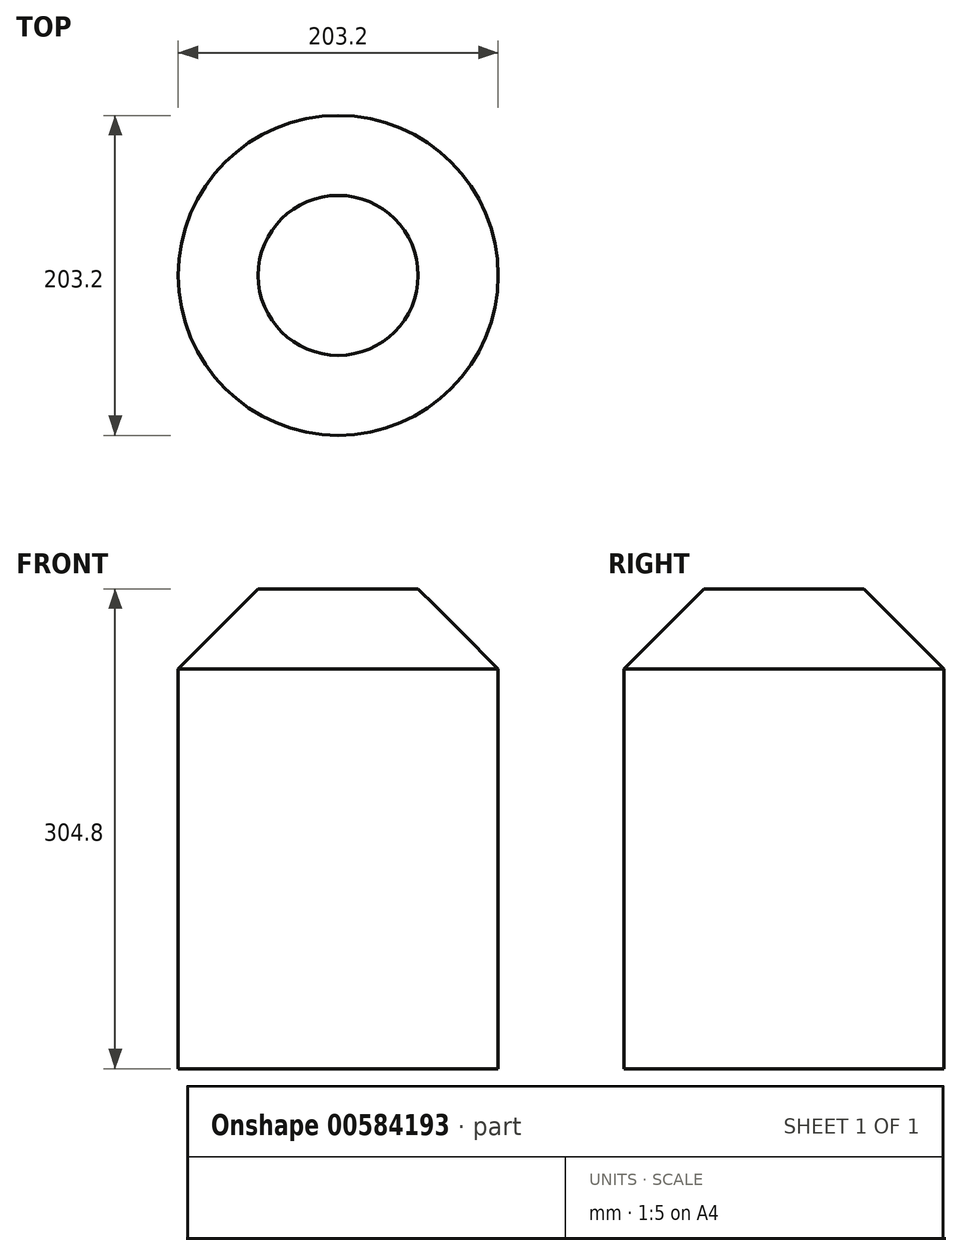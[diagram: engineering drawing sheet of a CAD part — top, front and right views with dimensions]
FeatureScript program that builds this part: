
annotation { "Feature Type Name" : "Feature", "Feature Type Description" : "" }
export const myFeature = defineFeature(function(context is Context, id is Id, definition is map)
    precondition{}
    {
        {
            var Q0;
            Q0=qCreatedBy(makeId("Top.planeOp"),FACE);
            var sketch = newSketch(context, id + "F0", { "sketchPlane" : qUnion([Q0])});
            skLineSegment(sketch, "E0.bottom", {"start": v(-254, 508) * mm, "end": v(254, 508) * mm});
            skLineSegment(sketch, "E0.top", {"start": v(-254, -508) * mm, "end": v(254, -508) * mm});
            skLineSegment(sketch, "E0.left", {"start": v(-254, 508) * mm, "end": v(-254, -508) * mm});
            skLineSegment(sketch, "E0.right", {"start": v(254, 508) * mm, "end": v(254, -508) * mm});
            skPoint(sketch, "E0.middle", {"position": v(0, 0) * mm});
            skLineSegment(sketch, "E1.bottom", {"start": v(-254, 508) * mm, "end": v(50.8, 508) * mm});
            skLineSegment(sketch, "E1.top", {"start": v(-254, 381) * mm, "end": v(50.8, 381) * mm});
            skLineSegment(sketch, "E1.left", {"start": v(-254, 508) * mm, "end": v(-254, 381) * mm});
            skLineSegment(sketch, "E1.right", {"start": v(50.8, 508) * mm, "end": v(50.8, 381) * mm});
            skArc(sketch, "E2", {"start": v(50.8, 381) * mm, "mid": v(-175.68, -38.1) * mm, "end": v(-254, -508) * mm});
            skCircle(sketch, "E3", {"center": v(152.4, 345.46) * mm, "radius": 101.6 * mm});
            skSolve(sketch);
        }
        {
            var Q0;
            Q0=makeQuery(id+"F0.imprint","IMPRINT",FACE,{"disambiguationData":[TD([[makeQuery(id+"F0.imprint","IMPRINT",EDGE,{"derivedFrom":sQuery(id+"F0.wireOp",EDGE,"E3")}),1.0]])]});
            extrude(context, id + "F1", {"entities" : qUnion([Q0]), "depth" : 304.8 * mm, "offsetDistance" : 25.4 * mm});
        }
        {
            var Q0;
            Q0=makeQuery(id+"F1.opExtrude","CAP_EDGE",EDGE,{"disambiguationData":[OSD([sQuery(id+"F0.wireOp",EDGE,"E3")])],"isStart":false});
            chamfer(context, id + "F2", {"entities" : qUnion([Q0]), "width" : 50.8 * mm, "tangentPropagation" : true});
        }
    });
